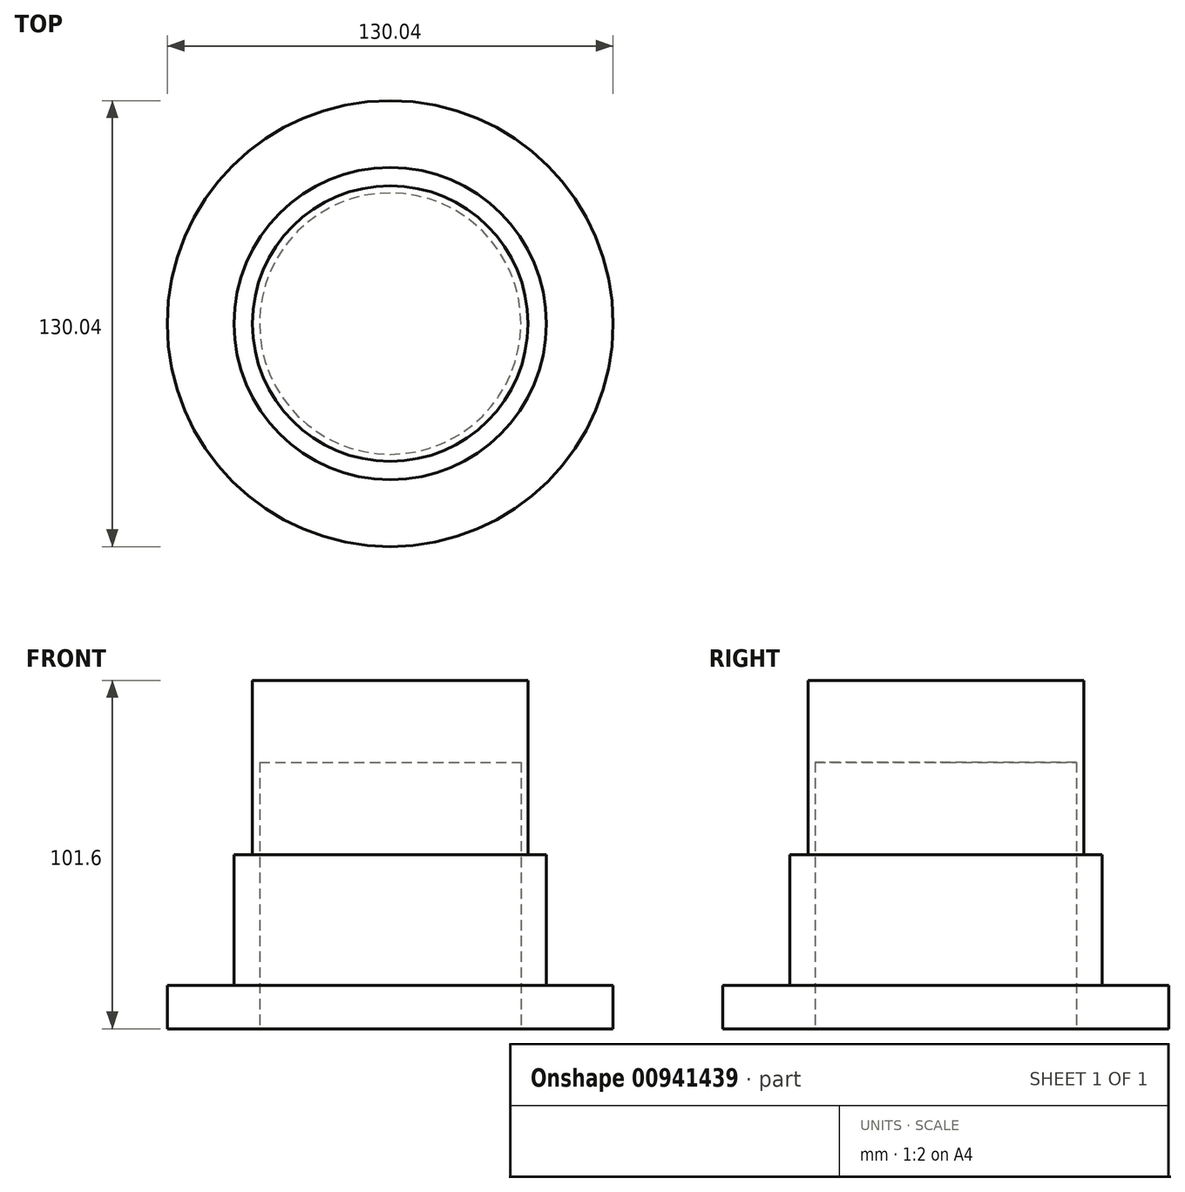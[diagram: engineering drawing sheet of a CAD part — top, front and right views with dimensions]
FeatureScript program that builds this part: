
annotation { "Feature Type Name" : "Feature", "Feature Type Description" : "" }
export const myFeature = defineFeature(function(context is Context, id is Id, definition is map)
    precondition{}
    {
        {
            var Q0;
            Q0=qCreatedBy(makeId("Top.planeOp"),FACE);
            var sketch = newSketch(context, id + "F0", { "sketchPlane" : qUnion([Q0])});
            skCircle(sketch, "E0", {"center": v(0, 0) * mm, "radius": 65.02 * mm});
            skSolve(sketch);
        }
        {
            var Q0;
            Q0=makeQuery(id+"F0.imprint","IMPRINT",FACE,{"disambiguationData":[TD([[makeQuery(id+"F0.imprint","IMPRINT",EDGE,{"derivedFrom":sQuery(id+"F0.wireOp",EDGE,"E0")}),1.0]])]});
            extrude(context, id + "F1", {"entities" : qUnion([Q0]), "depth" : 12.7 * mm, "offsetDistance" : 25.4 * mm});
        }
        {
            var Q0;
            Q0=makeQuery(id+"F1.opExtrude","CAP_FACE",FACE,{"disambiguationData":[OSD([sQuery(id+"F0.wireOp",EDGE,"E0")])],"isStart":false});
            var sketch = newSketch(context, id + "F2", { "sketchPlane" : qUnion([Q0])});
            skCircle(sketch, "E1", {"center": v(0, 0) * mm, "radius": 45.54 * mm});
            skSolve(sketch);
        }
        {
            var Q0;
            Q0=makeQuery(id+"F2.imprint","IMPRINT",FACE,{"disambiguationData":[TD([[makeQuery(id+"F2.imprint","IMPRINT",EDGE,{"derivedFrom":sQuery(id+"F2.wireOp",EDGE,"E1")}),1.0]])]});
            extrude(context, id + "F3", {"entities" : qUnion([Q0]), "operationType" : NewBodyOperationType.ADD, "depth" : 38.1 * mm, "offsetDistance" : 25.4 * mm});
        }
        {
            var Q0;
            Q0=makeQuery(id+"F3.opExtrude","CAP_FACE",FACE,{"disambiguationData":[OSD([sQuery(id+"F2.wireOp",EDGE,"E1")])],"isStart":false});
            var sketch = newSketch(context, id + "F4", { "sketchPlane" : qUnion([Q0])});
            skCircle(sketch, "E2", {"center": v(0, 0) * mm, "radius": 40.17 * mm});
            skSolve(sketch);
        }
        {
            var Q0;
            Q0=makeQuery(id+"F4.imprint","IMPRINT",FACE,{"disambiguationData":[TD([[makeQuery(id+"F4.imprint","IMPRINT",EDGE,{"derivedFrom":sQuery(id+"F4.wireOp",EDGE,"E2")}),1.0]])]});
            extrude(context, id + "F5", {"entities" : qUnion([Q0]), "operationType" : NewBodyOperationType.ADD, "depth" : 50.8 * mm, "offsetDistance" : 25.4 * mm});
        }
        {
            var Q0;
            Q0=makeQuery(id+"F1.opExtrude","CAP_FACE",FACE,{"disambiguationData":[OSD([sQuery(id+"F0.wireOp",EDGE,"E0")])],"isStart":true});
            var sketch = newSketch(context, id + "F6", { "sketchPlane" : qUnion([Q0])});
            skCircle(sketch, "E3", {"center": v(0, 0) * mm, "radius": 38.1 * mm});
            skSolve(sketch);
        }
        {
            var Q0;
            Q0=makeQuery(id+"F6.imprint","IMPRINT",FACE,{"disambiguationData":[TD([[makeQuery(id+"F6.imprint","IMPRINT",EDGE,{"derivedFrom":sQuery(id+"F6.wireOp",EDGE,"E3")}),1.0]])]});
            extrude(context, id + "F7", {"entities" : qUnion([Q0]), "operationType" : NewBodyOperationType.REMOVE, "oppositeDirection" : true, "depth" : 77.7 * mm, "offsetDistance" : 25.4 * mm});
        }
    });
